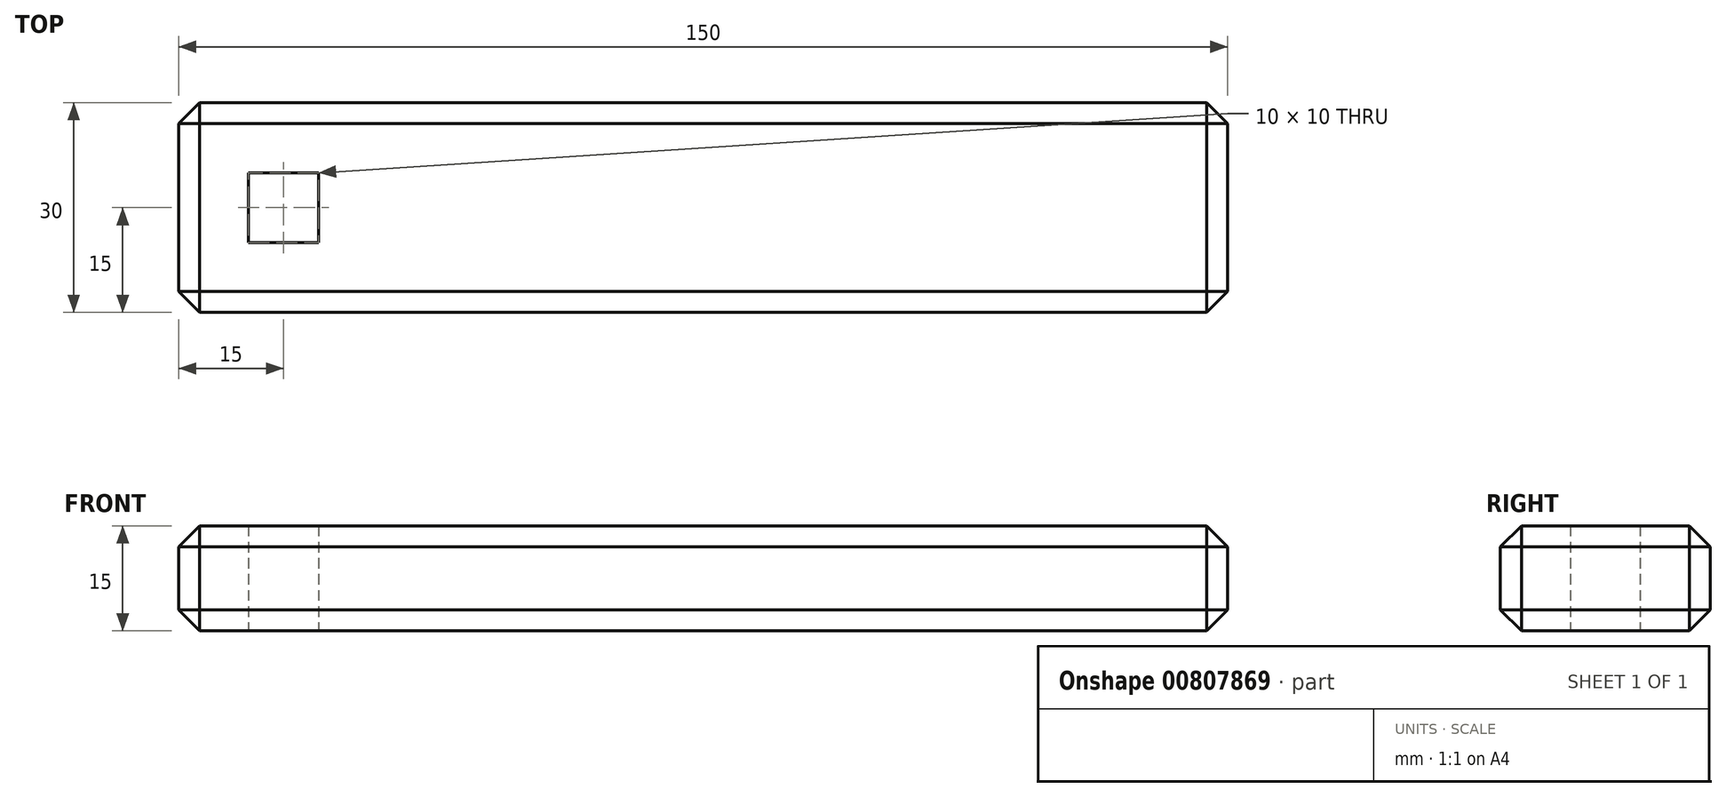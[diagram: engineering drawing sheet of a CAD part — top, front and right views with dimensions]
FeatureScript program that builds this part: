
annotation { "Feature Type Name" : "Feature", "Feature Type Description" : "" }
export const myFeature = defineFeature(function(context is Context, id is Id, definition is map)
    precondition{}
    {
        {
            var Q0;
            Q0=qCreatedBy(makeId("Top.planeOp"),FACE);
            var sketch = newSketch(context, id + "F0", { "sketchPlane" : qUnion([Q0])});
            skLineSegment(sketch, "E0.bottom", {"start": v(-5, -5) * mm, "end": v(5, -5) * mm});
            skLineSegment(sketch, "E0.top", {"start": v(-5, 5) * mm, "end": v(5, 5) * mm});
            skLineSegment(sketch, "E0.left", {"start": v(-5, -5) * mm, "end": v(-5, 5) * mm});
            skLineSegment(sketch, "E0.right", {"start": v(5, -5) * mm, "end": v(5, 5) * mm});
            skLineSegment(sketch, "E1.bottom", {"start": v(-15, 15) * mm, "end": v(135, 15) * mm});
            skLineSegment(sketch, "E1.top", {"start": v(-15, -15) * mm, "end": v(135, -15) * mm});
            skLineSegment(sketch, "E1.left", {"start": v(-15, 15) * mm, "end": v(-15, -15) * mm});
            skLineSegment(sketch, "E1.right", {"start": v(135, 15) * mm, "end": v(135, -15) * mm});
            skSolve(sketch);
        }
        {
            var Q0;
            Q0=makeQuery(id+"F0.imprint","IMPRINT",FACE,{"disambiguationData":[TD([[makeQuery(id+"F0.imprint","IMPRINT",EDGE,{"derivedFrom":sQuery(id+"F0.wireOp",EDGE,"E0.bottom")}),-1.0]])]});
            extrude(context, id + "F1", {"entities" : qUnion([Q0]), "depth" : 15 * mm, "offsetDistance" : 25 * mm});
        }
        {
            var Q0;
            Q0=makeQuery(id+"F1.opExtrude","CAP_EDGE",EDGE,{"disambiguationData":[OSD([sQuery(id+"F0.wireOp",EDGE,"E1.top")])],"isStart":false});
            var Q1;
            Q1=makeQuery(id+"F1.opExtrude","SWEPT_EDGE",EDGE,{"disambiguationData":[OSD([sQuery(id+"F0.wireOp",EDGE,"E1.top"),sQuery(id+"F0.wireOp",EDGE,"E1.right")])]});
            var Q2;
            Q2=makeQuery(id+"F1.opExtrude","CAP_EDGE",EDGE,{"disambiguationData":[OSD([sQuery(id+"F0.wireOp",EDGE,"E1.top")])],"isStart":true});
            var Q3;
            Q3=makeQuery(id+"F1.opExtrude","CAP_EDGE",EDGE,{"disambiguationData":[OSD([sQuery(id+"F0.wireOp",EDGE,"E1.right")])],"isStart":true});
            var Q4;
            Q4=makeQuery(id+"F1.opExtrude","SWEPT_EDGE",EDGE,{"disambiguationData":[OSD([sQuery(id+"F0.wireOp",EDGE,"E1.bottom"),sQuery(id+"F0.wireOp",EDGE,"E1.right")])]});
            var Q5;
            Q5=makeQuery(id+"F1.opExtrude","CAP_EDGE",EDGE,{"disambiguationData":[OSD([sQuery(id+"F0.wireOp",EDGE,"E1.right")])],"isStart":false});
            var Q6;
            Q6=makeQuery(id+"F1.opExtrude","CAP_EDGE",EDGE,{"disambiguationData":[OSD([sQuery(id+"F0.wireOp",EDGE,"E1.bottom")])],"isStart":false});
            var Q7;
            Q7=makeQuery(id+"F1.opExtrude","CAP_EDGE",EDGE,{"disambiguationData":[OSD([sQuery(id+"F0.wireOp",EDGE,"E1.left")])],"isStart":false});
            var Q8;
            Q8=makeQuery(id+"F1.opExtrude","SWEPT_EDGE",EDGE,{"disambiguationData":[OSD([sQuery(id+"F0.wireOp",EDGE,"E1.top"),sQuery(id+"F0.wireOp",EDGE,"E1.left")])]});
            var Q9;
            Q9=makeQuery(id+"F1.opExtrude","SWEPT_EDGE",EDGE,{"disambiguationData":[OSD([sQuery(id+"F0.wireOp",EDGE,"E1.bottom"),sQuery(id+"F0.wireOp",EDGE,"E1.left")])]});
            var Q10;
            Q10=makeQuery(id+"F1.opExtrude","CAP_EDGE",EDGE,{"disambiguationData":[OSD([sQuery(id+"F0.wireOp",EDGE,"E1.left")])],"isStart":true});
            var Q11;
            Q11=makeQuery(id+"F1.opExtrude","CAP_EDGE",EDGE,{"disambiguationData":[OSD([sQuery(id+"F0.wireOp",EDGE,"E1.bottom")])],"isStart":true});
            chamfer(context, id + "F2", {"entities" : qUnion([Q0, Q1, Q2, Q3, Q4, Q5, Q6, Q7, Q8, Q9, Q10, Q11]), "width" : 3 * mm, "tangentPropagation" : true});
        }
    });
